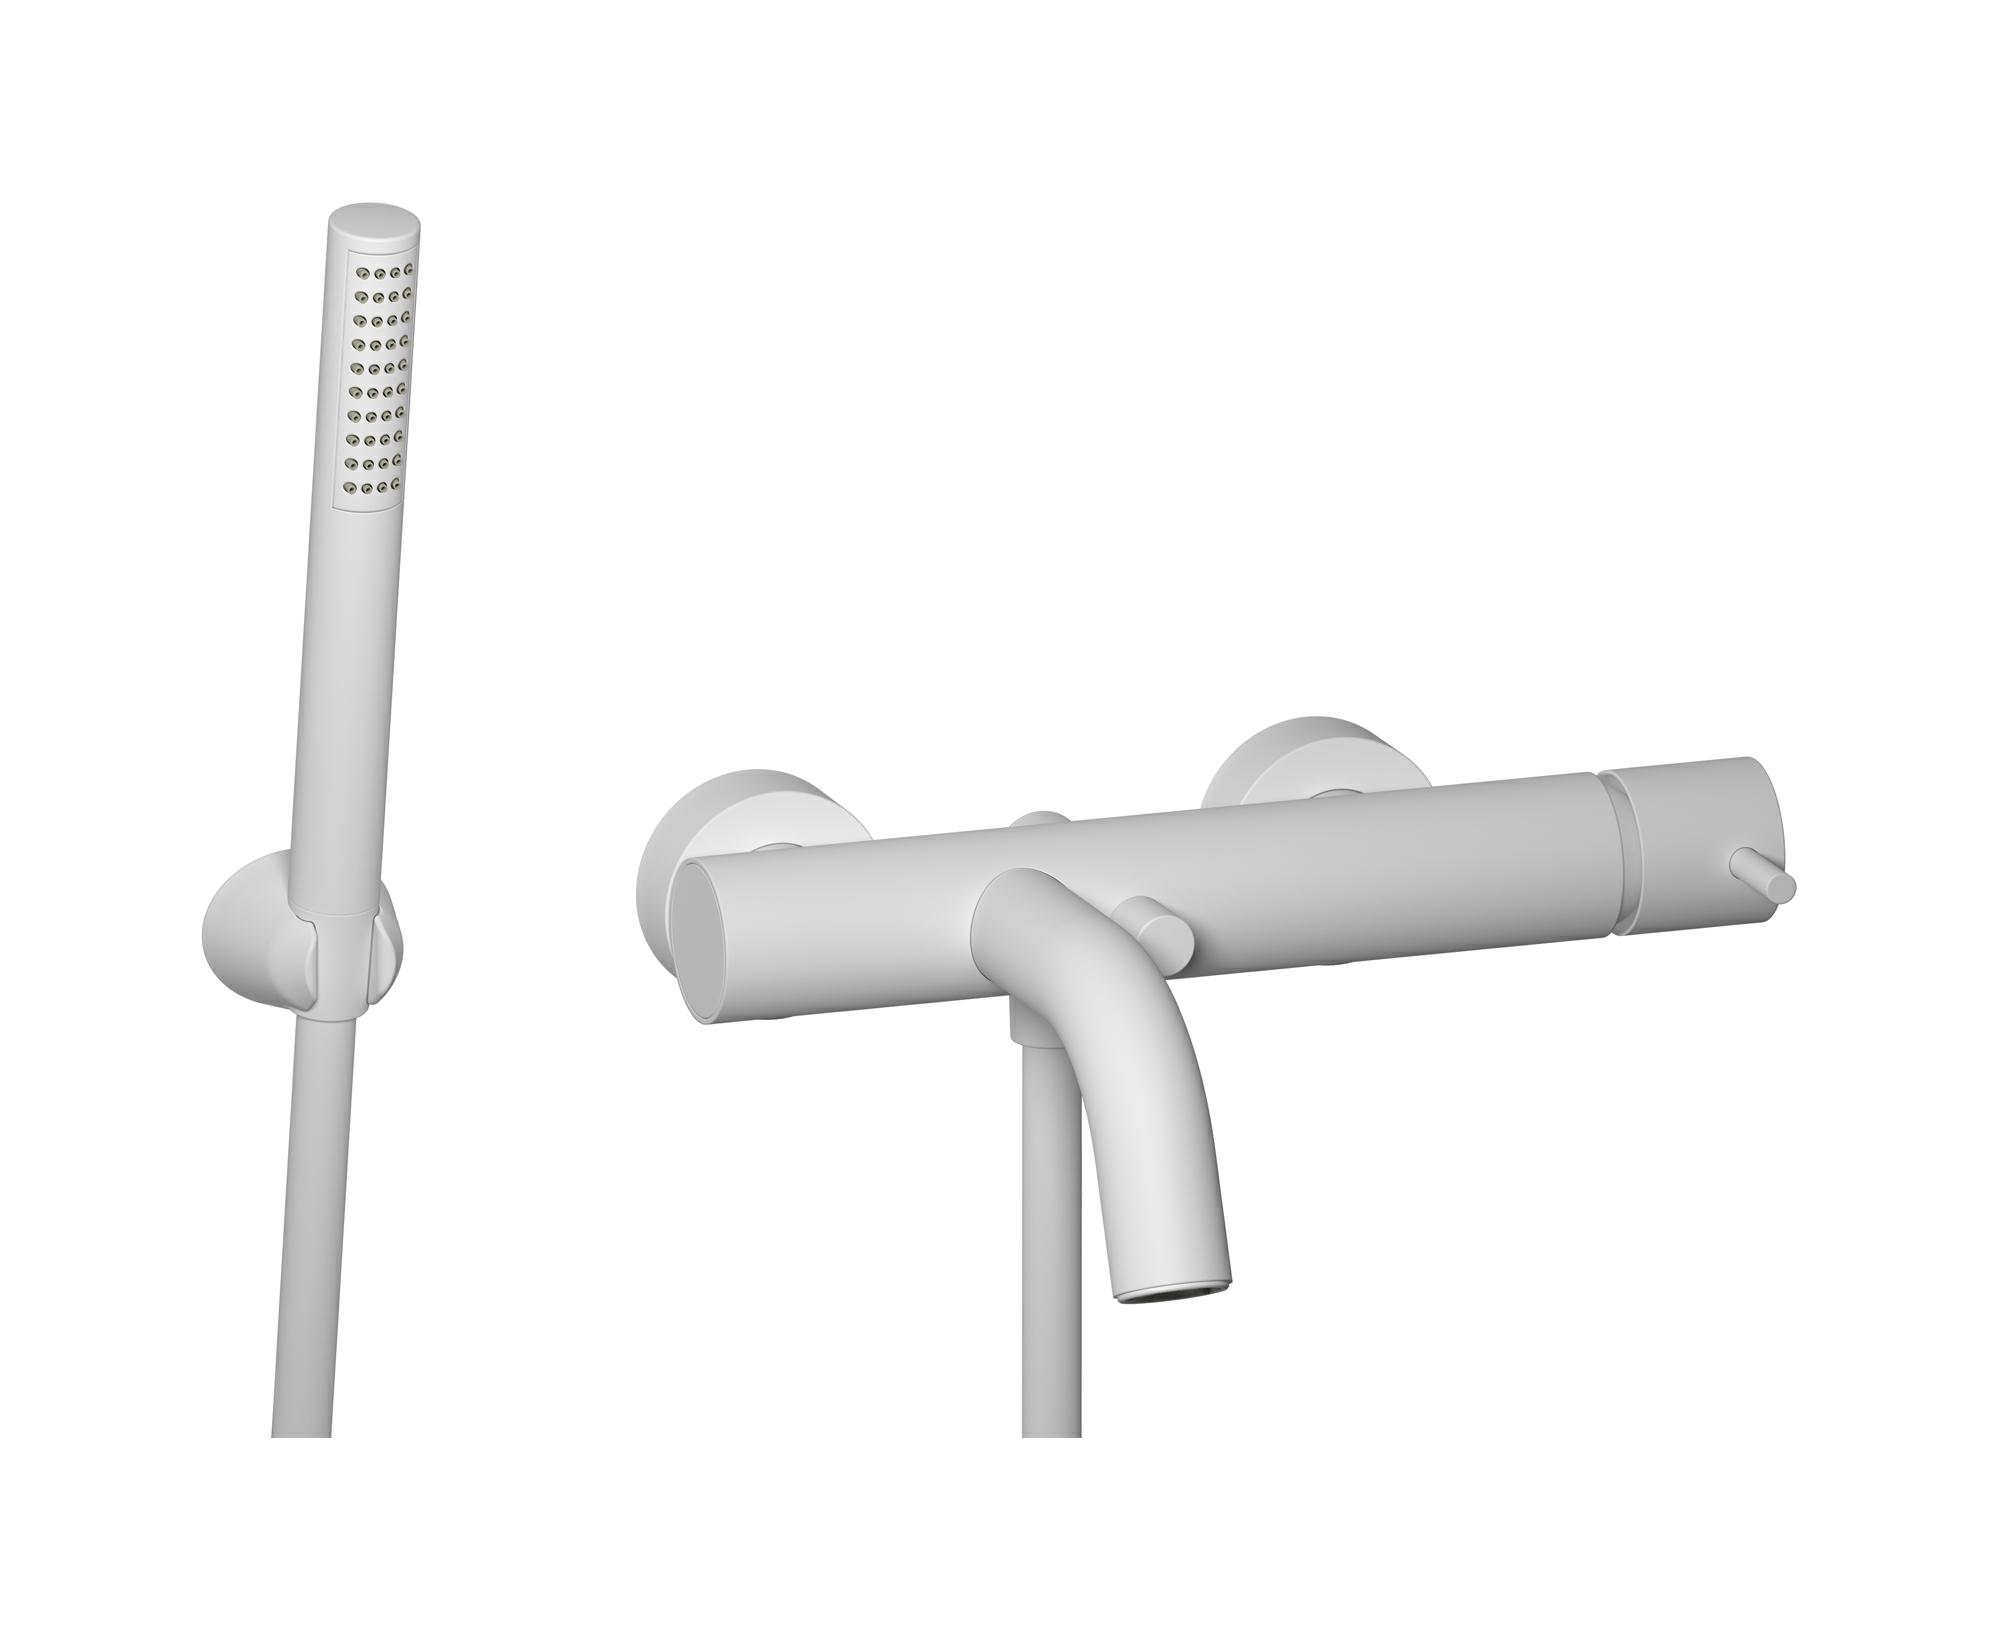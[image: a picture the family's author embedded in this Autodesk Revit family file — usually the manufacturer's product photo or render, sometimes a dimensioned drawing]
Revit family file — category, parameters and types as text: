
# Revit family: MT250
name_source: partatom
category: Apparecchi idraulici
units: mm (PartAtom-declared; Revit-internal decimal feet)

## family parameters
Basato su piano di lavoro = No
Condiviso = No
Mantieni orientamento annotazione = No
Numero OmniClass = 23.45.55.17
Punto di calcolo locali = No
Quota connettore circolare = Usa diametro
Sempre verticale = Sì
Taglio con vuoti quando caricato = No
Tipo di parte = Normale
Titolo OmniClass = Mixing Faucets

## types (13) — shared parameters
Cold water inlet = 10 mm  [stored 0.0328084 ft]
Commenti sul tipo = Bath filler
Connessione CW = No
Connessione HW = No
Connessione di scarico = No
Connessione di ventilazione = No
Descrizione = Wall mounted bath filler complete with shower kit
Hot water inlet = 10 mm  [stored 0.0328084 ft]
Produttore = IB Rubinetterie S.p.A.
URL = https://www.weareib.it
zero-valued in all types: Prospetto di default

## per-type parameters (varying)
| type | Finishes surface | Immagine tipo | Modello |
| Chrome | IB_Chrome | MT250CC.jpg | MT250CC |
| Brushed nickel | IB_Brushed nickel | MT250SS.jpg | MT250SS |
| Matt white | IB_matt white | MT250BO.jpg | MT250BO |
| Matt black | IB_matt black | MT250NP.jpg | MT250NP |
| Natural brass | IB_Brass | MT250ON.jpg | MT250ON |
| Black chrome | IB_Black chrome | MT250CF.jpg | MT250CF |
| Brushed black chrome | IB_Brushed black chrome | MT250CS.jpg | MT250CS |
| Pale gold | IB_Pale gold | MT250II.jpg | MT250II |
| Brushed pale gold | IB_brushed pale gold | MT250IS.jpg | MT250IS |
| Rose gold | IB_Rose gold | MT250RS.jpg | MT250RS |
| Brushed rose gold | IB_Brushed rose gold | MT250SR.jpg | MT250SR |
| Gold | IB_gold | MT250OO.jpg | MT250OO |
| Brushed gold | IB_brushed gold | MT250OS.jpg | MT250OS |

note: [stored X ft] marks values corroborated as IEEE doubles in the binary element streams (Revit-internal decimal feet)
